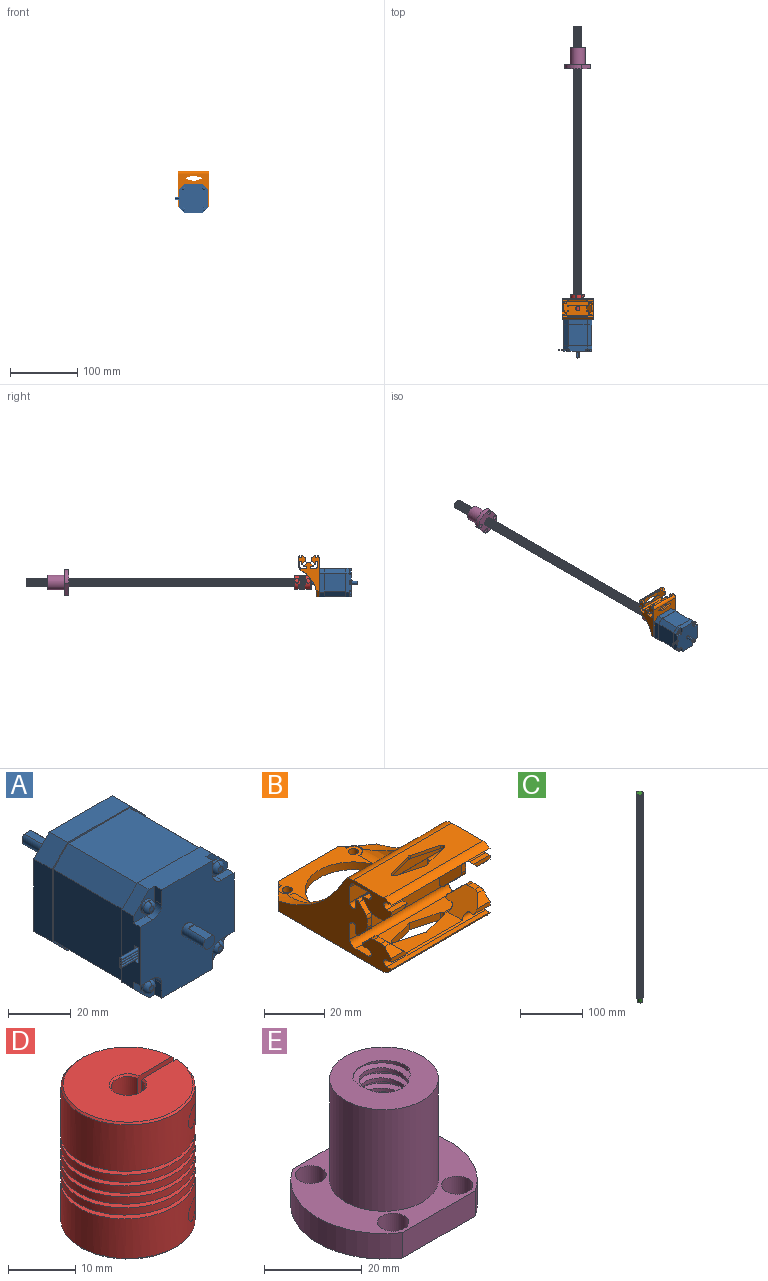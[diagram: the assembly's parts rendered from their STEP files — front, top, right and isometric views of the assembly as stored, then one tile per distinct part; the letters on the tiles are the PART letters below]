
ASSEMBLY  parts=5 mates=4
PART A: 93 faces, bbox 49.3x82x42.3 mm
  f0: plane 42.3x42.3mm, normal (0,1,0), area 858.8mm2, adj f1,f13,f15,f17,f19,f21,f32,f34
  f1: plane 8.25x7mm, normal (0.71,0,0.71), area 81.7mm2, adj f0,f3,f21,f34
  f2: plane 7x7mm, normal (0.71,0,0.71), area 52mm2, adj f12,f22,f23,f35
  f3: plane 42.3x42.3mm, normal (0,-1,0), area 75.6mm2, adj f1,f4,f5,f6,f7,f8,f9,f10
  f4: plane 31.5x6.71mm, normal (0.71,0,0.71), area 298.8mm2, adj f3,f5,f11,f12
  f5: plane 31.5x27.89mm, normal (1,0,0), area 878.4mm2, adj f3,f4,f6,f12
  f6: plane 31.5x6.71mm, normal (0.71,0,-0.71), area 298.8mm2, adj f3,f5,f7,f12
  f7: plane 31.5x27.89mm, normal (0,0,-1), area 878.4mm2, adj f3,f6,f8,f12
  f8: plane 31.5x6.71mm, normal (-0.71,0,-0.71), area 298.8mm2, adj f3,f7,f9,f12
  f9: plane 31.5x27.89mm, normal (-1,0,0), area 878.4mm2, adj f3,f8,f10,f12
  f10: plane 31.5x6.71mm, normal (-0.71,0,0.71), area 298.8mm2, adj f3,f9,f11,f12
  f11: plane 31.5x27.89mm, normal (0,0,1), area 878.4mm2, adj f3,f4,f10,f12
  f12: plane 42.3x42.3mm, normal (0,1,0), area 75.6mm2, adj f2,f4,f5,f6,f7,f8,f9,f10
  f13: plane 28.3x8.25mm, normal (-1,0,0), area 233.5mm2, adj f0,f3,f15,f32
  f14: plane 28.3x8.25mm, normal (-1,0,0), area 207.1mm2, adj f12,f16,f27,f29,f31,f33,f49,f50
  f15: plane 8.25x7mm, normal (-0.71,0,-0.71), area 81.7mm2, adj f0,f3,f13,f17
  f16: plane 7x7mm, normal (-0.71,0,-0.71), area 52mm2, adj f12,f14,f18,f49
  f17: plane 28.3x8.25mm, normal (0,0,-1), area 233.5mm2, adj f0,f3,f15,f19
  f18: plane 28.3x8.25mm, normal (0,0,-1), area 217.6mm2, adj f12,f16,f20,f27,f41,f42,f48,f49
  f19: plane 8.25x7mm, normal (0.71,0,-0.71), area 81.7mm2, adj f0,f3,f17,f21
  f20: plane 7x7mm, normal (0.71,0,-0.71), area 52mm2, adj f12,f18,f22,f41
  f21: plane 28.3x8.25mm, normal (1,0,0), area 233.5mm2, adj f0,f1,f3,f19
  f22: plane 28.3x8.25mm, normal (1,0,0), area 217.6mm2, adj f2,f12,f20,f23,f26,f27,f40,f41
  f23: plane 9.65x9.65mm, normal (0,-1,0), area 46.4mm2, adj f2,f22,f24,f25,f26,f35,f60
  f24: plane 5.65x3mm, normal (1,0,0), area 17mm2, adj f23,f25,f27,f35
  f25: cylinder r=4mm len=4mm, axis (0,1,0), area 18.8mm2, adj f23,f24,f26,f27
  f26: plane 5.65x3mm, normal (0,0,1), area 17mm2, adj f22,f23,f25,f27
  f27: plane 42.3x42.3mm, normal (0,-1,0), area 1410.9mm2, adj f14,f18,f22,f24,f25,f26,f28,f30
  f28: plane 5.65x3mm, normal (-1,0,0), area 17mm2, adj f27,f29,f30,f35
  f29: plane 9.65x9.65mm, normal (0,-1,0), area 46.4mm2, adj f14,f28,f30,f31,f33,f35,f36
  f30: cylinder r=4mm len=4mm, axis (0,-1,0), area 18.8mm2, adj f27,f28,f29,f31
  f31: plane 5.65x3mm, normal (0,0,1), area 17mm2, adj f14,f27,f29,f30
  f32: plane 8.25x7mm, normal (-0.71,0,0.71), area 81.7mm2, adj f0,f3,f13,f34
  f33: plane 7x7mm, normal (-0.71,0,0.71), area 52mm2, adj f12,f14,f29,f35
  f34: plane 28.3x8.25mm, normal (0,0,1), area 233.5mm2, adj f0,f1,f3,f32
  f35: plane 28.3x8.25mm, normal (0,0,1), area 217.6mm2, adj f2,f12,f23,f24,f27,f28,f29,f33
  f36: cylinder r=2.45mm len=4.9mm, axis (0,-1,0), area 15.4mm2, adj f29,f37,f39
  f37: torus R=0.95mm, axis (0,-1,0), area 14.1mm2, adj f36,f38,f39
  f38: plane 1.9x1.9mm, normal (0,-1,0), area 2.8mm2, adj f37,f39
  f39: torus R=0.95mm, axis (0,-1,0), area 14.1mm2, adj f36,f37,f38
  f40: plane 5.65x3mm, normal (0,0,-1), area 17mm2, adj f22,f27,f41,f43
  f41: plane 9.65x9.65mm, normal (0,-1,0), area 46.4mm2, adj f18,f20,f22,f40,f42,f43,f44
  f42: plane 5.65x3mm, normal (1,0,0), area 17mm2, adj f18,f27,f41,f43
  f43: cylinder r=4mm len=4mm, axis (0,-1,0), area 18.8mm2, adj f27,f40,f41,f42
  f44: cylinder r=2.45mm len=4.9mm, axis (0,-1,0), area 15.4mm2, adj f41,f45,f47
  f45: torus R=0.95mm, axis (0,-1,0), area 14.1mm2, adj f44,f46,f47
  f46: plane 1.9x1.9mm, normal (0,-1,0), area 2.8mm2, adj f45,f47
  f47: torus R=0.95mm, axis (0,-1,0), area 14.1mm2, adj f44,f45,f46
  f48: plane 5.65x3mm, normal (-1,0,0), area 17mm2, adj f18,f27,f49,f51
  f49: plane 9.65x9.65mm, normal (0,-1,0), area 46.4mm2, adj f14,f16,f18,f48,f50,f51,f52
  f50: plane 5.65x3mm, normal (0,0,-1), area 17mm2, adj f14,f27,f49,f51
  f51: cylinder r=4mm len=4mm, axis (0,1,0), area 18.8mm2, adj f27,f48,f49,f50
  f52: cylinder r=2.45mm len=4.9mm, axis (0,1,0), area 15.4mm2, adj f49,f53,f55
  f53: torus R=0.95mm, axis (0,1,0), area 14.1mm2, adj f52,f54,f55
  f54: plane 1.9x1.9mm, normal (0,-1,0), area 2.8mm2, adj f53,f55
  f55: torus R=0.95mm, axis (0,1,0), area 14.1mm2, adj f52,f53,f54
  f56: cylinder r=2.5mm len=10mm, axis (0,-1,0), area 131.3mm2, adj f27,f57,f58,f59
  f57: plane 8x3mm, normal (0,0,1), area 24mm2, adj f56,f58,f59
  f58: plane 5x4.5mm, normal (0,-1,0), area 18.6mm2, adj f56,f57
  f59: plane 3x0.5mm, normal (0,-1,0), area 1mm2, adj f56,f57
  f60: cylinder r=2.45mm len=4.9mm, axis (0,1,0), area 15.4mm2, adj f23,f61,f63
  f61: torus R=0.95mm, axis (0,1,0), area 14.1mm2, adj f60,f62,f63
  f62: plane 1.9x1.9mm, normal (0,-1,0), area 2.8mm2, adj f61,f63
  f63: torus R=0.95mm, axis (0,1,0), area 14.1mm2, adj f60,f61,f62
  f64: plane 3x1.75mm, normal (0,0,1), area 5.3mm2, adj f14,f65,f67,f68
  f65: plane 6x3mm, normal (0,-1,0), area 18mm2, adj f14,f64,f66,f68
  f66: plane 3x1.75mm, normal (0,0,-1), area 5.3mm2, adj f14,f65,f67,f68
  f67: plane 6x3mm, normal (0,1,0), area 18mm2, adj f14,f64,f66,f68
  f68: plane 6x1.75mm, normal (-1,0,0), area 7.6mm2, adj f64,f65,f66,f67,f69,f71,f73,f75
  f69: cylinder r=0.48mm len=10mm, axis (-1,0,0), area 30mm2, adj f68,f70
  f70: plane 0.96x0.96mm, normal (-1,0,0), area 0.7mm2, adj f69
  f71: cylinder r=0.48mm len=10mm, axis (-1,0,0), area 30mm2, adj f68,f72
  f72: plane 0.96x0.96mm, normal (-1,0,0), area 0.7mm2, adj f71
  f73: cylinder r=0.48mm len=10mm, axis (-1,0,0), area 30mm2, adj f68,f74
  f74: plane 0.96x0.96mm, normal (-1,0,0), area 0.7mm2, adj f73
  f75: cylinder r=0.48mm len=10mm, axis (-1,0,0), area 30mm2, adj f68,f76
  f76: plane 0.96x0.96mm, normal (-1,0,0), area 0.7mm2, adj f75
  f77: cylinder r=1.5mm len=4.5mm, axis (0,-1,0), area 42.4mm2, adj f0,f78
  f78: plane 3x3mm, normal (0,1,0), area 7.1mm2, adj f77
  f79: cylinder r=1.5mm len=4.5mm, axis (0,1,0), area 42.4mm2, adj f0,f80
  f80: plane 3x3mm, normal (0,1,0), area 7.1mm2, adj f79
  f81: cylinder r=1.5mm len=4.5mm, axis (0,1,0), area 42.4mm2, adj f0,f82
  f82: plane 3x3mm, normal (0,1,0), area 7.1mm2, adj f81
  f83: cylinder r=1.5mm len=4.5mm, axis (0,-1,0), area 42.4mm2, adj f0,f84
  f84: plane 3x3mm, normal (0,1,0), area 7.1mm2, adj f83
  f85: cylinder r=16mm len=32mm, axis (0,1,0), area 40.2mm2, adj f0,f86
  f86: plane 32x32mm, normal (0,1,0), area 424.1mm2, adj f85,f87
  f87: cylinder r=11mm len=22mm, axis (0,1,0), area 165.9mm2, adj f86,f88
  f88: plane 22x22mm, normal (0,1,0), area 360.5mm2, adj f87,f89
  f89: cylinder r=2.5mm len=22mm, axis (0,1,0), area 297.3mm2, adj f88,f90,f91,f92
  f90: plane 3x0.5mm, normal (0,1,0), area 1mm2, adj f89,f91
  f91: plane 15x3mm, normal (0,0,1), area 45mm2, adj f89,f90,f92
  f92: plane 5x4.5mm, normal (0,1,0), area 18.6mm2, adj f89,f91
PART B: 135 faces, bbox 47.1x62.8x30.9 mm
  f0: cylinder r=1.4mm len=11.38mm, axis (1,0,0), area 40.8mm2, adj f41,f57,f59,f110,f115,f127
  f1: cylinder r=1.4mm len=11.38mm, axis (1,0,0), area 40.8mm2, adj f41,f75,f77,f107,f114,f130
  f2: plane 7.5x1.61mm, normal (0,-1,0), area 10.7mm2, adj f41,f83,f84,f114
  f3: plane 7.5x1.61mm, normal (0,-1,0), area 10.7mm2, adj f41,f50,f51,f115
  f4: plane 7.5x2.03mm, normal (0,0,1), area 15.2mm2, adj f38,f43,f49,f111
  f5: plane 5.89x3.16mm, normal (0,-0.71,-0.71), area 19.3mm2, adj f6,f38,f43,f111
  f6: cylinder r=2.75mm len=2.73mm, axis (1,0,0), area 4.2mm2, adj f5,f7,f38,f111
  f7: plane 3.24x2.22mm, normal (0,0,-1), area 7.2mm2, adj f6,f8,f38,f111
  f8: cylinder r=2.75mm len=2.73mm, axis (1,0,0), area 4.2mm2, adj f7,f9,f38,f111
  f9: plane 6.06x3.33mm, normal (0,0.71,-0.71), area 20.7mm2, adj f8,f10,f38,f111
  f10: cylinder r=0.72mm len=7.5mm, axis (1,0,0), area 14.9mm2, adj f9,f11,f38,f111
  f11: plane 7.5x2.14mm, normal (0,0,1), area 16mm2, adj f10,f38,f58,f111
  f12: plane 7.2x2.13mm, normal (0,1,0), area 15.3mm2, adj f13,f38,f62,f112
  f13: cylinder r=0.72mm len=7.2mm, axis (1,0,0), area 14.3mm2, adj f12,f14,f38,f112
  f14: plane 5.76x3.33mm, normal (0,-0.71,0.71), area 19.3mm2, adj f13,f15,f38,f112
  f15: cylinder r=2.75mm len=2.43mm, axis (1,0,0), area 3.6mm2, adj f14,f16,f38,f108,f112
  f16: plane 3.24x2mm, normal (0,-1,0), area 6.5mm2, adj f15,f17,f38,f108
  f17: cylinder r=2.75mm len=3.09mm, axis (1,0,0), area 6.3mm2, adj f16,f18,f38,f108,f112
  f18: plane 5.76x2.67mm, normal (0,-0.71,-0.71), area 16.7mm2, adj f17,f19,f38,f112
  f19: cylinder r=0.72mm len=7.2mm, axis (1,0,0), area 14.3mm2, adj f18,f20,f38,f112
  f20: plane 7.2x2.13mm, normal (0,1,0), area 15.3mm2, adj f19,f21,f38,f112
  f21: cylinder r=1.4mm len=10mm, axis (1,0,0), area 37.8mm2, adj f20,f38,f73,f112
  f22: plane 7.5x2.13mm, normal (0,0,-1), area 16mm2, adj f23,f38,f76,f113
  f23: cylinder r=0.72mm len=7.5mm, axis (1,0,0), area 14.9mm2, adj f22,f24,f38,f113
  f24: plane 6.06x3.33mm, normal (0,0.71,0.71), area 20.7mm2, adj f23,f25,f38,f113
  f25: cylinder r=2.75mm len=2.73mm, axis (1,0,0), area 4.2mm2, adj f24,f26,f38,f113
  f26: plane 3.24x2.22mm, normal (0,0,1), area 7.2mm2, adj f25,f27,f38,f113
  f27: cylinder r=2.75mm len=2.73mm, axis (1,0,0), area 4.2mm2, adj f26,f28,f38,f113
  f28: plane 5.89x3.16mm, normal (0,-0.71,0.71), area 19.3mm2, adj f27,f38,f42,f113
  f29: plane 7.5x2.03mm, normal (0,0,-1), area 15.2mm2, adj f38,f42,f85,f113
  f30: cylinder r=1.7mm len=3.4mm, axis (0,0,-1), area 33.9mm2, adj f37,f46
  f31: cylinder r=1.7mm len=3.4mm, axis (0,0,-1), area 33.9mm2, adj f34,f46
  f32: cylinder r=1.7mm len=3.4mm, axis (0,0,-1), area 33.9mm2, adj f40,f46
  f33: cylinder r=1.7mm len=3.4mm, axis (0,0,-1), area 33.9mm2, adj f40,f46
  f34: plane 13.35x12.54mm, normal (0,0,1), area 46.3mm2, adj f31,f35,f45,f98,f103
  f35: cylinder r=6mm len=28.38mm, axis (0,1,0), area 205.2mm2, adj f34,f40,f45,f87,f90,f99,f103,f105
  f36: cylinder r=6mm len=1.74mm, axis (0,-1,0), area 1.1mm2, adj f40,f89,f106,f133
  f37: plane 13.35x12.54mm, normal (0,0,1), area 46.3mm2, adj f30,f45,f91,f96,f104
  f38: plane 53x30.18mm, normal (1,0,0), area 754.6mm2, adj f4,f5,f6,f7,f8,f9,f10,f11
  f39: plane 30.3x21.02mm, normal (0,1,0), area 601.9mm2, adj f92,f94,f96,f97,f98,f100,f117
  f40: plane 37x16mm, normal (0,0,1), area 257.9mm2, adj f32,f33,f35,f36,f44,f45,f91,f93
  f41: plane 53x30.18mm, normal (-1,0,0), area 754.6mm2, adj f0,f1,f2,f3,f46,f47,f48,f49
  f42: plane 7.5x1.61mm, normal (0,-1,0), area 10.7mm2, adj f28,f29,f38,f113
  f43: plane 7.5x1.61mm, normal (0,-1,0), area 10.7mm2, adj f4,f5,f38,f111
  f44: plane 28.3x3.18mm, normal (0,1,0), area 89.9mm2, adj f40,f46,f133,f134
  f45: cylinder r=16mm len=32mm, axis (0,0,-1), area 319.2mm2, adj f34,f35,f37,f40,f46,f91,f97
  f46: plane 57.47x46.3mm, normal (0,0,-1), area 1624.3mm2, adj f30,f31,f32,f33,f38,f41,f44,f45
  f47: plane 46.3x14.48mm, normal (0,0,1), area 555.3mm2, adj f38,f41,f100,f101,f118,f119,f120,f121
  f48: plane 46.3x2.03mm, normal (0,0,-1), area 93.8mm2, adj f38,f41,f49,f101
  f49: cylinder r=1.4mm len=46.3mm, axis (1,0,0), area 103.6mm2, adj f4,f38,f41,f48,f50,f110,f111,f115
  f50: plane 7.5x2.03mm, normal (0,0,1), area 15.2mm2, adj f3,f41,f49,f115
  f51: plane 5.89x3.16mm, normal (0,-0.71,-0.71), area 19.3mm2, adj f3,f41,f52,f115
  f52: cylinder r=2.75mm len=2.73mm, axis (1,0,0), area 4.2mm2, adj f41,f51,f53,f115
  f53: plane 3.24x2.22mm, normal (0,0,-1), area 7.2mm2, adj f41,f52,f54,f115
  f54: cylinder r=2.75mm len=2.73mm, axis (1,0,0), area 4.2mm2, adj f41,f53,f55,f115
  f55: plane 6.06x3.33mm, normal (0,0.71,-0.71), area 20.7mm2, adj f41,f54,f56,f115
  f56: cylinder r=0.72mm len=7.5mm, axis (1,0,0), area 14.9mm2, adj f41,f55,f57,f115
  f57: plane 7.5x2.14mm, normal (0,0,1), area 16mm2, adj f0,f41,f56,f115
  f58: cylinder r=1.4mm len=11.38mm, axis (1,0,0), area 40.8mm2, adj f11,f38,f59,f110,f111,f128
  f59: plane 46.3x6.22mm, normal (0,0,-1), area 233.1mm2, adj f0,f38,f41,f58,f60,f120,f121,f126
  f60: cylinder r=2.4mm len=46.3mm, axis (1,0,0), area 177.1mm2, adj f38,f41,f59,f61
  f61: plane 46.3x6.22mm, normal (0,-1,0), area 288.1mm2, adj f38,f41,f60,f62
  f62: cylinder r=1.4mm len=46.3mm, axis (1,0,0), area 77.7mm2, adj f12,f38,f41,f61,f63,f73,f112,f116
  f63: plane 7.2x2.13mm, normal (0,1,0), area 15.3mm2, adj f41,f62,f64,f116
  f64: cylinder r=0.72mm len=7.2mm, axis (1,0,0), area 14.3mm2, adj f41,f63,f65,f116
  f65: plane 5.76x3.33mm, normal (0,-0.71,0.71), area 19.3mm2, adj f41,f64,f66,f116
  f66: cylinder r=2.75mm len=2.43mm, axis (1,0,0), area 3.6mm2, adj f41,f65,f67,f109,f116
  f67: plane 3.24x2mm, normal (0,-1,0), area 6.5mm2, adj f41,f66,f68,f109
  f68: cylinder r=2.75mm len=3.09mm, axis (1,0,0), area 6.3mm2, adj f41,f67,f69,f109,f116
  f69: plane 5.76x2.67mm, normal (0,-0.71,-0.71), area 16.7mm2, adj f41,f68,f70,f116
  f70: cylinder r=0.72mm len=7.2mm, axis (1,0,0), area 14.3mm2, adj f41,f69,f71,f116
  f71: plane 7.2x2.13mm, normal (0,1,0), area 15.3mm2, adj f41,f70,f72,f116
  f72: cylinder r=1.4mm len=10mm, axis (1,0,0), area 37.8mm2, adj f41,f71,f73,f116
  f73: plane 46.3x14.87mm, normal (0,-1,0), area 483.8mm2, adj f21,f38,f41,f62,f72,f74,f112,f116
  f74: cylinder r=2.4mm len=46.3mm, axis (1,0,0), area 177.1mm2, adj f38,f41,f73,f75
  f75: plane 46.3x6.22mm, normal (0,0,1), area 233.1mm2, adj f1,f38,f41,f74,f76,f122,f123,f130
  f76: cylinder r=1.4mm len=11.38mm, axis (1,0,0), area 40.8mm2, adj f22,f38,f75,f107,f113,f132
  f77: plane 7.5x2.13mm, normal (0,0,-1), area 16mm2, adj f1,f41,f78,f114
  f78: cylinder r=0.72mm len=7.5mm, axis (1,0,0), area 14.9mm2, adj f41,f77,f79,f114
  f79: plane 6.06x3.33mm, normal (0,0.71,0.71), area 20.7mm2, adj f41,f78,f80,f114
  f80: cylinder r=2.75mm len=2.73mm, axis (1,0,0), area 4.2mm2, adj f41,f79,f81,f114
  f81: plane 3.24x2.22mm, normal (0,0,1), area 7.2mm2, adj f41,f80,f82,f114
  f82: cylinder r=2.75mm len=2.73mm, axis (1,0,0), area 4.2mm2, adj f41,f81,f83,f114
  f83: plane 5.89x3.16mm, normal (0,-0.71,0.71), area 19.3mm2, adj f2,f41,f82,f114
  f84: plane 7.5x2.03mm, normal (0,0,-1), area 15.2mm2, adj f2,f41,f85,f114
  f85: cylinder r=1.4mm len=46.3mm, axis (1,0,0), area 103.6mm2, adj f29,f38,f41,f84,f86,f107,f113,f114
  f86: plane 46.3x2.03mm, normal (0,0,1), area 93.8mm2, adj f38,f41,f85,f102
  f87: plane 12.79x11.02mm, normal (1,0,0), area 61.5mm2, adj f35,f90,f94
  f88: plane 12.79x11.02mm, normal (-1,0,0), area 61.5mm2, adj f89,f91,f92
  f89: cylinder r=45mm len=38.01mm, axis (1,0,0), area 113.1mm2, adj f36,f38,f88,f91,f92,f100,f106,f133
  f90: cylinder r=45mm len=38.01mm, axis (1,0,0), area 113.1mm2, adj f35,f41,f87,f93,f94,f100,f105,f134
  f91: cylinder r=6mm len=28.38mm, axis (0,-1,0), area 205.2mm2, adj f37,f40,f45,f88,f89,f95,f104,f106
  f92: cylinder r=6mm len=20.88mm, axis (0,0,-1), area 160.6mm2, adj f39,f88,f89,f95,f100
  f93: cylinder r=6mm len=1.74mm, axis (0,1,0), area 1.1mm2, adj f40,f90,f105,f134
  f94: cylinder r=6mm len=20.88mm, axis (0,0,1), area 160.6mm2, adj f39,f87,f90,f99,f100
  f95: bspline ~7.42x6mm, area 34.4mm2, adj f91,f92,f96,f104
  f96: cylinder r=5mm len=9.19mm, axis (-1,0,0), area 67mm2, adj f37,f39,f95,f97,f104
  f97: bspline ~14.98x5.95mm, area 84.3mm2, adj f39,f45,f96,f98
  f98: cylinder r=5mm len=9.19mm, axis (-1,0,0), area 67mm2, adj f34,f39,f97,f99,f103
  f99: bspline ~6.36x6mm, area 40.4mm2, adj f35,f94,f98,f103
  f100: cylinder r=5mm len=46.3mm, axis (1,0,0), area 183.2mm2, adj f38,f39,f41,f47,f89,f90,f92,f94
  f101: cylinder r=5mm len=46.3mm, axis (-1,0,0), area 171.1mm2, adj f38,f41,f47,f48
  f102: cylinder r=5mm len=46.3mm, axis (-1,0,0), area 262.3mm2, adj f38,f41,f46,f86
  f103: cylinder r=3mm len=6mm, axis (0,0,1), area 13.3mm2, adj f34,f35,f98,f99
  f104: cylinder r=3mm len=6mm, axis (0,0,1), area 13.3mm2, adj f37,f91,f95,f96
  f105: cylinder r=3mm len=6mm, axis (0,0,1), area 3.3mm2, adj f35,f40,f90,f93
  f106: cylinder r=3mm len=6mm, axis (0,0,1), area 3.3mm2, adj f36,f40,f89,f91
  f107: plane 26.3x6.97mm, normal (0,0,1), area 143.8mm2, adj f1,f76,f85,f113,f114,f124,f125,f130
  f108: plane 4.5x0.07mm, normal (-1,0,0), area 0.3mm2, adj f15,f16,f17,f112
  f109: plane 4.5x0.07mm, normal (1,0,0), area 0.3mm2, adj f66,f67,f68,f116
  f110: plane 26.3x6.97mm, normal (0,0,-1), area 143.8mm2, adj f0,f49,f58,f111,f115,f118,f119,f127
  f111: plane 14.33x8.54mm, normal (-0.71,0,-0.71), area 99.5mm2, adj f4,f5,f6,f7,f8,f9,f10,f11
  f112: plane 15.01x8.62mm, normal (-0.71,-0.71,0), area 103.6mm2, adj f12,f13,f14,f15,f17,f18,f19,f20
  f113: plane 14.33x8.54mm, normal (-0.71,0,0.71), area 99.5mm2, adj f22,f23,f24,f25,f26,f27,f28,f29
  f114: plane 14.33x8.54mm, normal (0.71,0,0.71), area 99.5mm2, adj f1,f2,f77,f78,f79,f80,f81,f82
  f115: plane 14.33x8.54mm, normal (0.71,0,-0.71), area 99.5mm2, adj f0,f3,f49,f50,f51,f52,f53,f54
  f116: plane 15.01x8.62mm, normal (0.71,-0.71,0), area 103.6mm2, adj f62,f63,f64,f65,f66,f68,f69,f70
  f117: cylinder r=3.17mm len=6.35mm, axis (0,1,0), area 32.6mm2, adj f39,f73
  f118: plane 11.12x2.97mm, normal (-0.26,0.97,0), area 18.4mm2, adj f47,f110,f128,f129
  f119: plane 11.12x2.97mm, normal (0.26,0.97,0), area 18.4mm2, adj f47,f110,f127,f129
  f120: plane 11.12x2.97mm, normal (0.26,-0.97,0), area 15mm2, adj f47,f59,f126,f127
  f121: plane 11.12x2.97mm, normal (-0.26,-0.97,0), area 15mm2, adj f47,f59,f126,f128
  f122: plane 11.38x3.03mm, normal (-0.26,-0.97,0), area 33.9mm2, adj f46,f75,f123,f132
  f123: plane 11.38x3.03mm, normal (0.26,-0.97,0), area 33.9mm2, adj f46,f75,f122,f130
  f124: plane 11.12x3.18mm, normal (0.26,0.97,0), area 36.5mm2, adj f46,f107,f130,f131
  f125: plane 11.12x3.18mm, normal (-0.26,0.97,0), area 36.5mm2, adj f46,f107,f131,f132
  f126: cylinder r=1mm len=1.31mm, axis (0,0,-1), area 0.7mm2, adj f47,f59,f120,f121
  f127: cylinder r=1mm len=1.93mm, axis (0,0,-1), area 3.7mm2, adj f0,f47,f59,f110,f119,f120
  f128: cylinder r=1mm len=1.93mm, axis (0,0,-1), area 3.7mm2, adj f47,f58,f59,f110,f118,f121
  f129: cylinder r=1mm len=1.6mm, axis (0,0,-1), area 0.8mm2, adj f47,f110,f118,f119
  f130: cylinder r=1mm len=3.18mm, axis (0,0,-1), area 7.8mm2, adj f1,f46,f75,f107,f123,f124
  f131: cylinder r=1mm len=3.18mm, axis (0,0,-1), area 1.7mm2, adj f46,f107,f124,f125
  f132: cylinder r=1mm len=3.18mm, axis (0,0,-1), area 7.8mm2, adj f46,f75,f76,f107,f122,f125
  f133: plane 9.04x9.04mm, normal (0.71,0.71,0), area 44.5mm2, adj f36,f38,f40,f44,f46,f89
  f134: plane 9.04x9.04mm, normal (-0.71,0.71,0), area 44.5mm2, adj f40,f41,f44,f46,f90,f93
PART C: 10 faces, bbox 12.7x14.7x410 mm
  f0: cylinder r=6.35mm len=400.05mm, axis (0,0,-1), area -4638.8mm2, adj f1,f2,f5,f7,f8,f9
  f1: plane 12.7x12.28mm, normal (0,0,-1), area 64.9mm2, adj f0,f3,f5,f6,f7
  f2: plane 12.7x12.29mm, normal (0,0,1), area 115.2mm2, adj f0,f6,f8,f9
  f3: cylinder r=4mm len=9.53mm, axis (0,0,1), area 239.4mm2, adj f1,f4
  f4: plane 8x8mm, normal (0,0,-1), area 50.3mm2, adj f3
  f5: plane 1.27x0.8mm, normal (0,-1,0), area 0.8mm2, adj f0,f1,f6,f9
  f6: cylinder r=5.08mm len=400.05mm, axis (0,0,1), area 12611.1mm2, adj f1,f2,f5,f7,f8,f9
  f7: bspline ~399.96x14.66mm, area 7450.8mm2, adj f0,f1,f6,f8
  f8: plane 1.27x0.8mm, normal (0,-1,0), area 0.8mm2, adj f0,f2,f6,f7
  f9: bspline ~399.96x14.66mm, area 7483.9mm2, adj f0,f2,f5,f6
PART D: 32 faces, bbox 24.4x23.3x26.3 mm
  f0: cone r=4mm half-angle=45deg, axis (0,0,-1), area 10.7mm2, adj f1,f2,f3,f4
  f1: plane 9.63x7.31mm, normal (0,-1,0), area 42.2mm2, adj f0,f2,f4,f5,f6,f7,f8
  f2: plane 19.4x19.39mm, normal (0,0,-1), area 232.6mm2, adj f0,f1,f3,f5
  f3: plane 9.58x7.31mm, normal (0,1,0), area 41.9mm2, adj f0,f2,f4,f5,f6,f9,f10
  f4: cylinder r=4mm len=12.2mm, axis (0,0,-1), area 244.1mm2, adj f0,f1,f3,f7,f8,f9,f10,f11
  f5: cone r=10mm half-angle=45deg, axis (0,0,1), area 25.9mm2, adj f1,f2,f3,f6
  f6: cylinder r=10mm len=24.4mm, axis (0,0,1), area 1299.1mm2, adj f1,f3,f5,f7,f10,f11,f12,f14
  f7: bspline ~23.13x22mm, area 1185.7mm2, adj f1,f4,f6,f13,f18,f19
  f8: cylinder r=1.7mm len=5.75mm, axis (0,1,0), area 57.2mm2, adj f1,f4,f20
  f9: cylinder r=1.7mm len=8.99mm, axis (0,1,0), area 82.2mm2, adj f3,f4,f21
  f10: bspline ~23.13x22mm, area 195mm2, adj f3,f4,f6,f11
  f11: plane 6x0.7mm, normal (-1,0,0), area 4.2mm2, adj f4,f6,f10,f12
  f12: bspline ~23.13x22mm, area 1319.3mm2, adj f4,f6,f11,f13,f14,f19
  f13: plane 8x7.24mm, normal (0,0,-1), area 19.9mm2, adj f4,f7,f12,f19
  f14: plane 8.92x8.39mm, normal (0,1,0), area 51.3mm2, adj f6,f12,f15,f19,f22,f23,f24
  f15: cone r=9.7mm half-angle=45deg, axis (0,0,-1), area 25.9mm2, adj f6,f14,f16,f23
  f16: plane 8.85x8.39mm, normal (0,-1,0), area 50.9mm2, adj f6,f15,f17,f19,f22,f23,f25
  f17: bspline ~14.4x11.57mm, area 69.1mm2, adj f6,f16,f18,f19
  f18: plane 7.5x0.7mm, normal (1,0,0), area 5.2mm2, adj f6,f7,f17,f19
  f19: cylinder r=2.5mm len=12.2mm, axis (0,0,1), area 159.1mm2, adj f7,f12,f13,f14,f16,f17,f18,f22
  f20: plane 6x5.85mm, normal (0,1,0), area 19mm2, adj f8,f26,f27
  f21: cylinder r=10mm len=3.4mm, axis (0,0,1), area 10.5mm2, adj f9
  f22: cone r=2.5mm half-angle=45deg, axis (0,0,1), area 6.7mm2, adj f14,f16,f19,f23
  f23: plane 19.4x19.39mm, normal (0,0,1), area 264.7mm2, adj f14,f15,f16,f22
  f24: cylinder r=1.7mm len=8.21mm, axis (0,1,0), area 83.7mm2, adj f14,f28
  f25: cylinder r=1.7mm len=5.75mm, axis (0,1,0), area 61.4mm2, adj f16,f29
  f26: cylinder r=10mm len=6mm, axis (0,0,1), area 30.3mm2, adj f20,f27
  f27: cylinder r=3mm len=6mm, axis (0,1,0), area 32.4mm2, adj f20,f26
  f28: cylinder r=10mm len=3.4mm, axis (0,0,1), area 10.5mm2, adj f24
  f29: plane 6x5.85mm, normal (0,1,0), area 19mm2, adj f25,f30,f31
  f30: cylinder r=10mm len=6mm, axis (0,0,1), area 30.3mm2, adj f29,f31
  f31: cylinder r=3mm len=6mm, axis (0,1,0), area 32.4mm2, adj f29,f30
PART E: 29 faces, bbox 38.4x32.1x32.8 mm
  f0: bspline ~31.23x14.66mm, area 563.7mm2, adj f2,f14,f15,f16,f17,f18,f19,f20
  f1: bspline ~30.39x14.66mm, area 539.1mm2, adj f2,f14,f15,f16,f17,f18,f19,f20
  f2: cylinder r=5.08mm len=30.15mm, axis (0,0,-1), area 304.8mm2, adj f0,f1,f14,f28
  f3: cylinder r=19.05mm len=31.75mm, axis (0,0,-1), area 238.3mm2, adj f4,f10,f11,f12
  f4: plane 21.06x6.35mm, normal (0,1,0), area 133.7mm2, adj f3,f5,f11,f12
  f5: cylinder r=19.05mm len=31.75mm, axis (0,0,-1), area 238.3mm2, adj f4,f10,f11,f12
  f6: cylinder r=3.17mm len=6.35mm, axis (0,0,-1), area 126.7mm2, adj f11,f12
  f7: cylinder r=3.17mm len=6.35mm, axis (0,0,-1), area 126.7mm2, adj f11,f12
  f8: cylinder r=3.17mm len=6.35mm, axis (0,0,-1), area 126.7mm2, adj f11,f12
  f9: cylinder r=3.17mm len=6.35mm, axis (0,0,-1), area 126.7mm2, adj f11,f12
  f10: plane 21.06x6.35mm, normal (0,-1,0), area 133.7mm2, adj f3,f5,f11,f12
  f11: plane 38.1x31.75mm, normal (0,0,1), area 534.7mm2, adj f3,f4,f5,f6,f7,f8,f9,f10
  f12: plane 38.1x31.75mm, normal (0,0,-1), area 796mm2, adj f3,f4,f5,f6,f7,f8,f9,f10
  f13: cylinder r=11.11mm len=25.4mm, axis (0,0,-1), area 1773.5mm2, adj f11,f14
  f14: plane 22.54x22.54mm, normal (0,0,1), area 284.3mm2, adj f0,f1,f2,f13,f27
  f15: cylinder r=6.35mm len=12.7mm, axis (0,0,1), area 37.7mm2, adj f0,f1,f16,f27
  f16: cylinder r=6.35mm len=12.7mm, axis (0,0,1), area 37.6mm2, adj f0,f1,f15,f17
  f17: cylinder r=6.35mm len=12.7mm, axis (0,0,1), area 37.6mm2, adj f0,f1,f16,f18
  f18: cylinder r=6.35mm len=12.7mm, axis (0,0,1), area 37.7mm2, adj f0,f1,f17,f19
  f19: cylinder r=6.35mm len=12.7mm, axis (0,0,1), area 37.6mm2, adj f0,f1,f18,f20
  f20: cylinder r=6.35mm len=12.7mm, axis (0,0,1), area 37.7mm2, adj f0,f1,f19,f21
  f21: cylinder r=6.35mm len=12.7mm, axis (0,0,1), area 37.7mm2, adj f0,f1,f20,f22
  f22: cylinder r=6.35mm len=12.7mm, axis (0,0,1), area 37.6mm2, adj f0,f1,f21,f23
  f23: cylinder r=6.35mm len=12.7mm, axis (0,0,1), area 37.7mm2, adj f0,f1,f22,f24
  f24: cylinder r=6.35mm len=12.7mm, axis (0,0,1), area 37.7mm2, adj f0,f1,f23,f25
  f25: cylinder r=6.35mm len=12.7mm, axis (0,0,1), area 37.6mm2, adj f0,f1,f24,f26
  f26: cylinder r=6.35mm len=12.7mm, axis (0,0,1), area 101.4mm2, adj f0,f12,f25,f28
  f27: cylinder r=6.35mm len=10.78mm, axis (0,0,1), area 7mm2, adj f1,f14,f15
  f28: plane 1.6x1.27mm, normal (0,-1,0), area 1.6mm2, adj f0,f1,f2,f26
PLACE A t=(45.85,-450.85,25.85)mm fixed
PLACE B rot(axis=(-1,0,0),90deg) t=(45.85,-450.85,25.85)mm
PLACE C rot(axis=(-0.1,0.7,0.7),168.4deg) t=(45.81,-414.33,25.99)mm
PLACE D rot(axis=(0.47,-0.63,0.63),129.9deg) t=(45.81,-438.85,25.99)mm
PLACE E rot(axis=(-0.32,-0.67,-0.67),144.7deg) t=(45.81,-78.25,25.99)mm
MATE revolute D.f23 <-> A.f56  axis (0,-1,0) through (45.85,-438.85,25.85)mm
MATE fastened D.f0 <-> C.f3  axis (0,1,0) through (45.81,-413.85,25.99)mm
MATE cylindrical E.f2 <-> C.f0  axis (0,-1,0) through (45.81,-78.25,25.99)mm
MATE fastened B.f45 <-> A.f56  axis (0,-1,0) through (45.85,-450.85,25.85)mm
